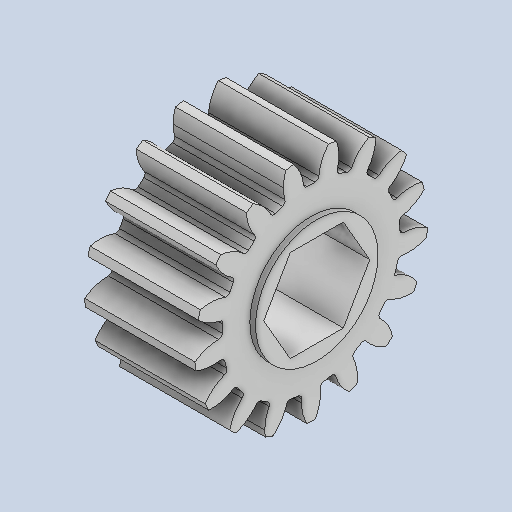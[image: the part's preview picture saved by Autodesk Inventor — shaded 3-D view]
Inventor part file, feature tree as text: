
AUTODESK INVENTOR PART (.ipt)
format: ipt  version: 2022.3 (Build 263350000, 350)  size: 296,448 bytes
history: native  units: in
note: dims shown in document units (in); Inventor stores cm internally (conversion verified against a paired STEP export)
features: fillet x1
ambient origin geometry x8: Origin, YZ Plane, XZ Plane, XY Plane, X Axis, Y Axis, Z Axis, Center Point
bodies: Solid1 (feature_tree)
feature tree (1):
  fillet  "Fillet1"  [1 undecoded]
note: 1 required parameter value undecoded (feature->parameter linkage not recoverable at this tier; creation-order binding heuristic only, values carry confidence <= 0.55)
